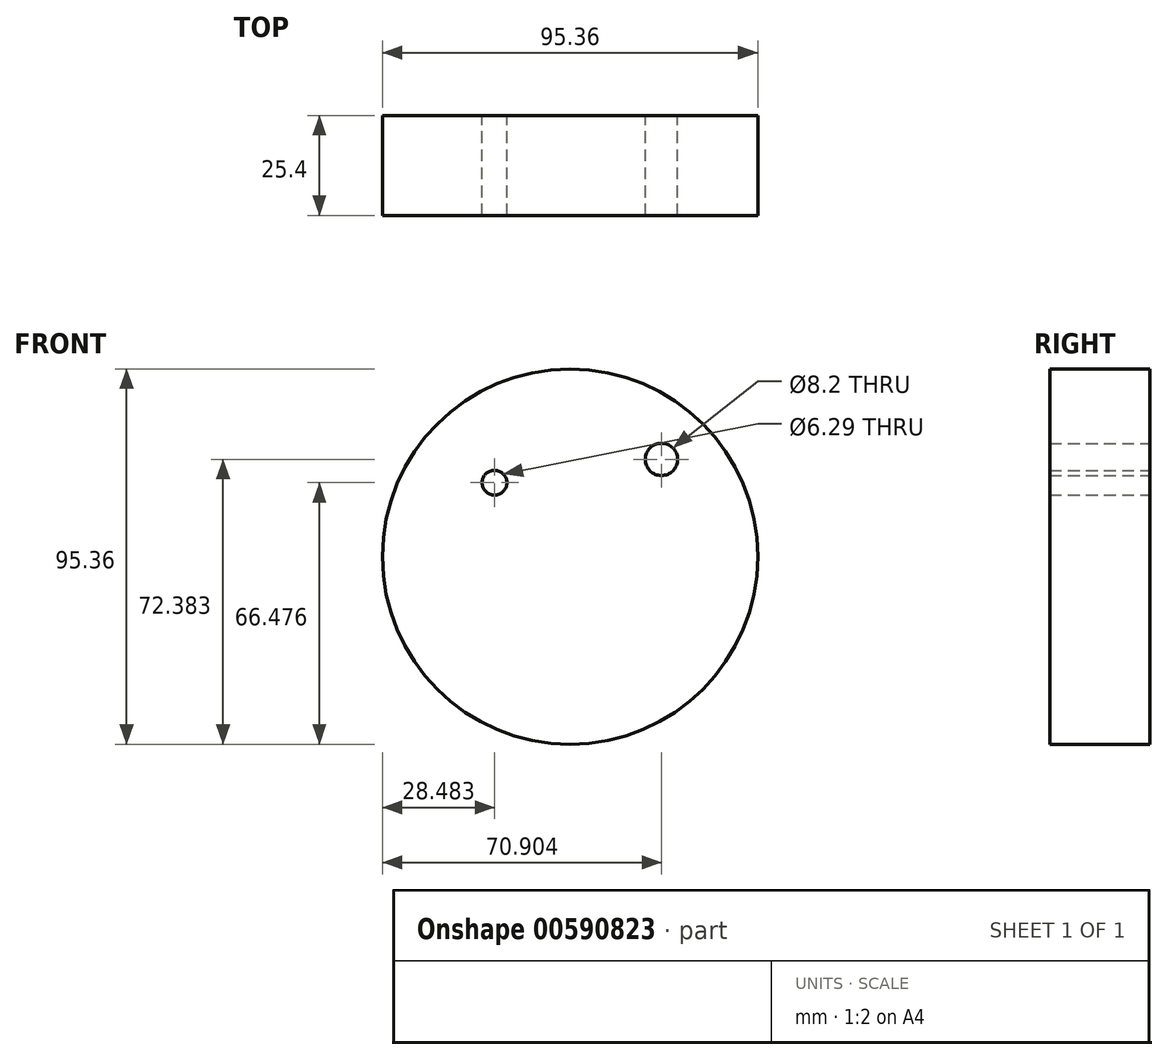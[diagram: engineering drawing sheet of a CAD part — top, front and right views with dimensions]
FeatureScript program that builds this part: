
annotation { "Feature Type Name" : "Feature", "Feature Type Description" : "" }
export const myFeature = defineFeature(function(context is Context, id is Id, definition is map)
    precondition{}
    {
        {
            var Q0;
            Q0=qCreatedBy(makeId("Front.planeOp"),FACE);
            var sketch = newSketch(context, id + "F0", { "sketchPlane" : qUnion([Q0])});
            skCircle(sketch, "E0", {"center": v(0, 7.65) * mm, "radius": 47.68 * mm});
            skSolve(sketch);
        }
        {
            var Q0;
            Q0=makeQuery(id+"F0.imprint","IMPRINT",FACE,{"disambiguationData":[TD([[makeQuery(id+"F0.imprint","IMPRINT",EDGE,{"derivedFrom":sQuery(id+"F0.wireOp",EDGE,"E0")}),1.0]])]});
            var sketch = newSketch(context, id + "F1", { "sketchPlane" : qUnion([Q0])});
            skCircle(sketch, "E1", {"center": v(-19.2, 26.45) * mm, "radius": 3.14 * mm});
            skCircle(sketch, "E2", {"center": v(23.22, 32.35) * mm, "radius": 4.1 * mm});
            skSolve(sketch);
        }
        {
            var Q0;
            Q0=makeQuery(id+"F1.imprint","IMPRINT",FACE,{"disambiguationData":[TD([[makeQuery(id+"F1.imprint","IMPRINT",EDGE,{"derivedFrom":sQuery(id+"F1.wireOp",EDGE,"E1")}),-1.0]])]});
            extrude(context, id + "F2", {"entities" : qUnion([Q0]), "depth" : 25.4 * mm, "offsetDistance" : 25.4 * mm});
        }
    });
